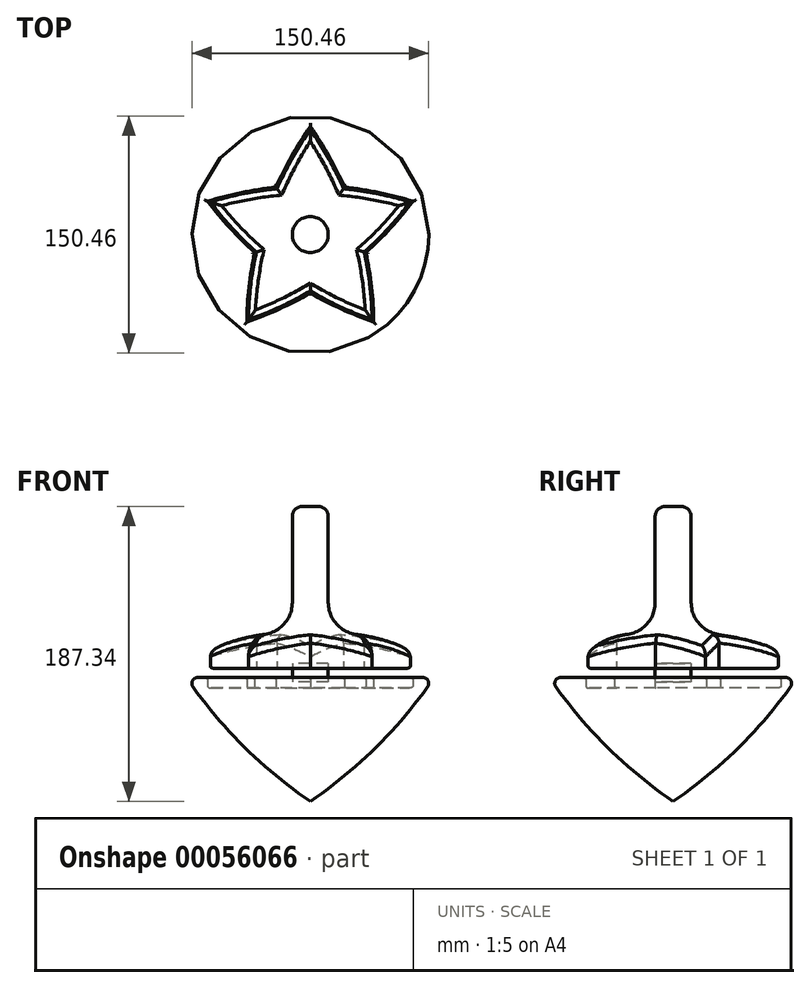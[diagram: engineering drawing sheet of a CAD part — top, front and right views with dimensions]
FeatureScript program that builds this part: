
annotation { "Feature Type Name" : "Feature", "Feature Type Description" : "" }
export const myFeature = defineFeature(function(context is Context, id is Id, definition is map)
    precondition{}
    {
        {
            var Q0;
            Q0=qCreatedBy(makeId("Top.planeOp"),FACE);
            var sketch = newSketch(context, id + "F0", { "sketchPlane" : qUnion([Q0])});
            skArc(sketch, "E0", {"start": v(39.25, -54.02) * mm, "mid": v(28.67, 9.31) * mm, "end": v(0, 66.77) * mm});
            skArc(sketch, "E1", {"start": v(0, 66.77) * mm, "mid": v(-28.67, 9.31) * mm, "end": v(-39.25, -54.02) * mm});
            skArc(sketch, "E2", {"start": v(63.5, 20.63) * mm, "mid": v(0, 30.14) * mm, "end": v(-63.5, 20.63) * mm});
            skArc(sketch, "E3", {"start": v(-63.5, 20.63) * mm, "mid": v(-17.72, -24.39) * mm, "end": v(39.25, -54.02) * mm});
            skArc(sketch, "E4", {"start": v(-39.25, -54.02) * mm, "mid": v(17.72, -24.39) * mm, "end": v(63.5, 20.63) * mm});
            skSolve(sketch);
        }
        {
            var Q0;
            Q0=qSketchRegion(id+"F0",true);
            extrude(context, id + "F1", {"entities" : qUnion([Q0]), "depth" : 67.5 * mm});
        }
        {
            var Q0;
            Q0=qCreatedBy(makeId("Top.planeOp"),FACE);
            var sketch = newSketch(context, id + "F2", { "sketchPlane" : qUnion([Q0])});
            skCircle(sketch, "E5", {"center": v(0, 0) * mm, "radius": 190.5 * mm});
            skLineSegment(sketch, "E6", {"start": v(0, 190.5) * mm, "end": v(0, -190.5) * mm});
            skSolve(sketch);
        }
        {
            var Q0;
            Q0=makeQuery(id+"F1.opExtrude","SWEPT_BODY",BODY,{"disambiguationData":[OSD([sQuery(id+"F0.wireOp",EDGE,"E0"),sQuery(id+"F0.wireOp",EDGE,"E1"),sQuery(id+"F0.wireOp",EDGE,"E2"),sQuery(id+"F0.wireOp",EDGE,"E3"),sQuery(id+"F0.wireOp",EDGE,"E4")])]});
            var Q1;
            Q1=makeQuery(id+"F1.opExtrude","SWEPT_EDGE",EDGE,{"disambiguationData":[OSD([sQuery(id+"F0.wireOp",EDGE,"E2"),sQuery(id+"F0.wireOp",EDGE,"E3")])]});
            var Q2;
            Q2=makeQuery(id+"F1.opExtrude","CAP_FACE",FACE,{"disambiguationData":[OSD([sQuery(id+"F0.wireOp",EDGE,"E0"),sQuery(id+"F0.wireOp",EDGE,"E1"),sQuery(id+"F0.wireOp",EDGE,"E2"),sQuery(id+"F0.wireOp",EDGE,"E3"),sQuery(id+"F0.wireOp",EDGE,"E4")])],"isStart":false});
            transform(context, id + "F3", {"entities" : qUnion([Q0]), "transformType" : TransformType.TRANSLATION_DISTANCE, "transformDirection" : qUnion([Q2]), "distance" : 166.71 * mm, "makeCopy" : false});
        }
        {
            var Q0;
            {var subQ0=sQuery(id+"F2.wireOp",EDGE,"E6");Q0=makeQuery(id+"F2.imprint","IMPRINT",FACE,{"disambiguationData":[TD([[makeQuery(id+"F2.imprint","IMPRINT",EDGE,{"derivedFrom":subQ0}),-1.0]])]});}
            var Q1;
            Q1=sQuery(id+"F2.wireOp",EDGE,"E6");
            revolve(context, id + "F4", {"entities" : qUnion([Q0]), "axis" : qUnion([Q1]), "revolveType" : RevolveType.FULL});
        }
        {
            var Q0;
            Q0=makeQuery(id+"F1.opExtrude","SWEPT_BODY",BODY,{"disambiguationData":[OSD([sQuery(id+"F0.wireOp",EDGE,"E0"),sQuery(id+"F0.wireOp",EDGE,"E1"),sQuery(id+"F0.wireOp",EDGE,"E2"),sQuery(id+"F0.wireOp",EDGE,"E3"),sQuery(id+"F0.wireOp",EDGE,"E4")])]});
            var Q1;
            Q1=makeQuery(id+"F4.opRevolve","SWEPT_BODY",BODY,{"disambiguationData":[OSD([sQuery(id+"F2.wireOp",EDGE,"E5"),sQuery(id+"F2.wireOp",EDGE,"E6")])]});
            booleanBodies(context, id + "F5", {"operationType" : BooleanOperationType.INTERSECTION, "tools" : qUnion([Q0, Q1])});
        }
        {
            var Q0;
            Q0=makeQuery(id+"F5.opBoolean","INTERSECT",BODY,{"derivedFrom":[makeQuery(id+"F1.opExtrude","SWEPT_BODY",BODY,{"disambiguationData":[OSD([sQuery(id+"F0.wireOp",EDGE,"E0"),sQuery(id+"F0.wireOp",EDGE,"E1"),sQuery(id+"F0.wireOp",EDGE,"E2"),sQuery(id+"F0.wireOp",EDGE,"E3"),sQuery(id+"F0.wireOp",EDGE,"E4")])]}),makeQuery(id+"F4.opRevolve","SWEPT_BODY",BODY,{"disambiguationData":[OSD([sQuery(id+"F2.wireOp",EDGE,"E5"),sQuery(id+"F2.wireOp",EDGE,"E6")])]})]});
            var Q1;
            Q1=qCreatedBy(makeId("Top.planeOp"),FACE);
            transform(context, id + "F6", {"entities" : qUnion([Q0]), "transformType" : TransformType.TRANSLATION_DISTANCE, "transformDirection" : qUnion([Q1]), "distance" : 160.87 * mm, "oppositeDirection" : true, "makeCopy" : false});
        }
        {
            var Q0;
            Q0=qCreatedBy(makeId("Top.planeOp"),FACE);
            var sketch = newSketch(context, id + "F7", { "sketchPlane" : qUnion([Q0])});
            skCircle(sketch, "E7", {"center": v(0, 0) * mm, "radius": 19.69 * mm});
            skSolve(sketch);
        }
        {
            var Q0;
            Q0=makeQuery(id+"F7.imprint","IMPRINT",FACE,{"disambiguationData":[TD([[makeQuery(id+"F7.imprint","IMPRINT",EDGE,{"derivedFrom":sQuery(id+"F7.wireOp",EDGE,"E7")}),1.0]])]});
            var Q1;
            Q1=sQuery(id+"F7.wireOp",EDGE,"E7");
            extrude(context, id + "F8", {"entities" : qUnion([Q0]), "surfaceEntities" : qUnion([Q1]), "depth" : 6.35 * mm});
        }
        {
            var Q0;
            Q0=makeQuery(id+"F8.opExtrude","SWEPT_BODY",BODY,{"disambiguationData":[OSD([sQuery(id+"F7.wireOp",EDGE,"E7")])]});
            var Q1;
            Q1=makeQuery(id+"F1.opExtrude","CAP_FACE",FACE,{"disambiguationData":[OSD([sQuery(id+"F0.wireOp",EDGE,"E0"),sQuery(id+"F0.wireOp",EDGE,"E1"),sQuery(id+"F0.wireOp",EDGE,"E2"),sQuery(id+"F0.wireOp",EDGE,"E3"),sQuery(id+"F0.wireOp",EDGE,"E4")])],"isStart":true});
            transform(context, id + "F9", {"entities" : qUnion([Q0]), "transformType" : TransformType.TRANSLATION_DISTANCE, "transformDirection" : qUnion([Q1]), "distance" : 52.24 * mm, "makeCopy" : false});
        }
        {
            var Q0;
            Q0=makeQuery(id+"F8.opExtrude","SWEPT_BODY",BODY,{"disambiguationData":[OSD([sQuery(id+"F7.wireOp",EDGE,"E7")])]});
            var Q1;
            Q1=makeQuery(id+"F5.opBoolean","INTERSECT",BODY,{"derivedFrom":[makeQuery(id+"F1.opExtrude","SWEPT_BODY",BODY,{"disambiguationData":[OSD([sQuery(id+"F0.wireOp",EDGE,"E0"),sQuery(id+"F0.wireOp",EDGE,"E1"),sQuery(id+"F0.wireOp",EDGE,"E2"),sQuery(id+"F0.wireOp",EDGE,"E3"),sQuery(id+"F0.wireOp",EDGE,"E4")])]}),makeQuery(id+"F4.opRevolve","SWEPT_BODY",BODY,{"disambiguationData":[OSD([sQuery(id+"F2.wireOp",EDGE,"E5"),sQuery(id+"F2.wireOp",EDGE,"E6")])]})]});
            booleanBodies(context, id + "F10", {"operationType" : BooleanOperationType.SUBTRACTION, "tools" : qUnion([Q0]), "targets" : qUnion([Q1])});
        }
        {
            var Q0;
            Q0=qCreatedBy(makeId("Front.planeOp"),FACE);
            var sketch = newSketch(context, id + "F11", { "sketchPlane" : qUnion([Q0])});
            skLineSegment(sketch, "E8", {"start": v(-78.74, 0) * mm, "end": v(78.74, 0) * mm});
            skArc(sketch, "E9", {"start": v(-78.74, 0) * mm, "mid": v(-43.07, -43.07) * mm, "end": v(0, -78.74) * mm});
            skLineSegment(sketch, "E10", {"start": v(0, -78.74) * mm, "end": v(0, 0) * mm});
            skSolve(sketch);
        }
        {
            var Q0;
            {var subQ0=sQuery(id+"F11.wireOp",EDGE,"E9");Q0=makeQuery(id+"F11.imprint","IMPRINT",FACE,{"disambiguationData":[TD([[makeQuery(id+"F11.imprint","IMPRINT",EDGE,{"derivedFrom":subQ0}),1.0]])]});}
            var Q1;
            Q1=sQuery(id+"F11.wireOp",EDGE,"E10");
            revolve(context, id + "F12", {"operationType" : NewBodyOperationType.ADD, "entities" : qUnion([Q0]), "axis" : qUnion([Q1]), "revolveType" : RevolveType.FULL});
        }
        {
            var Q0;
            Q0=qCreatedBy(makeId("Top.planeOp"),FACE);
            var sketch = newSketch(context, id + "F13", { "sketchPlane" : qUnion([Q0])});
            skCircle(sketch, "E11", {"center": v(0, 0) * mm, "radius": 11.43 * mm});
            skSolve(sketch);
        }
        {
            var Q0;
            Q0=makeQuery(id+"F13.imprint","IMPRINT",FACE,{"disambiguationData":[TD([[makeQuery(id+"F13.imprint","IMPRINT",EDGE,{"derivedFrom":sQuery(id+"F13.wireOp",EDGE,"E11")}),1.0]])]});
            extrude(context, id + "F14", {"entities" : qUnion([Q0]), "operationType" : NewBodyOperationType.ADD, "depth" : 108.6 * mm, "hasSecondDirection" : true, "secondDirectionOppositeDirection" : false, "secondDirectionDepth" : 8.63 * mm});
        }
        {
            var Q0;
            Q0=makeQuery(id+"F14.opExtrude","CAP_EDGE",EDGE,{"disambiguationData":[OSD([sQuery(id+"F13.wireOp",EDGE,"E11")])],"isStart":false});
            fillet(context, id + "F15", {"entities" : qUnion([Q0]), "radius" : 6.35 * mm, "tangentPropagation" : true, "allowEdgeOverflow" : false});
        }
        {
            var Q0;
            Q0=makeQuery(id+"F13.imprint","IMPRINT",FACE,{"disambiguationData":[TD([[makeQuery(id+"F13.imprint","IMPRINT",EDGE,{"derivedFrom":sQuery(id+"F13.wireOp",EDGE,"E11")}),1.0]])]});
            extrude(context, id + "F16", {"entities" : qUnion([Q0]), "depth" : 11.77 * mm});
        }
        {
            var Q0;
            Q0=makeQuery(id+"F16.opExtrude","SWEPT_BODY",BODY,{"disambiguationData":[OSD([sQuery(id+"F13.wireOp",EDGE,"E11")])]});
            transform(context, id + "F17", {"entities" : qUnion([Q0]), "transformType" : TransformType.TRANSLATION_3D, "dx" : 0 * mm, "dy" : 0 * mm, "dz" : -2.9 * mm, "makeCopy" : false});
        }
        {
            var Q0;
            Q0=makeQuery(id+"F16.opExtrude","SWEPT_BODY",BODY,{"disambiguationData":[OSD([sQuery(id+"F13.wireOp",EDGE,"E11")])]});
            transform(context, id + "F18", {"entities" : qUnion([Q0]), "transformType" : TransformType.TRANSLATION_3D, "dx" : 0 * mm, "dy" : 0 * mm, "dz" : 0 * mm, "makeCopy" : true});
        }
        {
            var Q0;
            Q0=makeQuery(id+"F5.opBoolean","INTERSECT",BODY,{"derivedFrom":[makeQuery(id+"F1.opExtrude","SWEPT_BODY",BODY,{"disambiguationData":[OSD([sQuery(id+"F0.wireOp",EDGE,"E0"),sQuery(id+"F0.wireOp",EDGE,"E1"),sQuery(id+"F0.wireOp",EDGE,"E2"),sQuery(id+"F0.wireOp",EDGE,"E3"),sQuery(id+"F0.wireOp",EDGE,"E4")])]}),makeQuery(id+"F4.opRevolve","SWEPT_BODY",BODY,{"disambiguationData":[OSD([sQuery(id+"F2.wireOp",EDGE,"E5"),sQuery(id+"F2.wireOp",EDGE,"E6")])]})]});
            transform(context, id + "F19", {"entities" : qUnion([Q0]), "transformType" : TransformType.TRANSLATION_3D, "dx" : 0 * mm, "dy" : 0 * mm, "dz" : -11.54 * mm, "makeCopy" : true});
        }
        {
            var Q0;
            Q0=makeQuery(id+"F19.opPattern","COPY",BODY,{"derivedFrom":makeQuery(id+"F5.opBoolean","INTERSECT",BODY,{"derivedFrom":[makeQuery(id+"F1.opExtrude","SWEPT_BODY",BODY,{"disambiguationData":[OSD([sQuery(id+"F0.wireOp",EDGE,"E0"),sQuery(id+"F0.wireOp",EDGE,"E1"),sQuery(id+"F0.wireOp",EDGE,"E2"),sQuery(id+"F0.wireOp",EDGE,"E3"),sQuery(id+"F0.wireOp",EDGE,"E4")])]}),makeQuery(id+"F4.opRevolve","SWEPT_BODY",BODY,{"disambiguationData":[OSD([sQuery(id+"F2.wireOp",EDGE,"E5"),sQuery(id+"F2.wireOp",EDGE,"E6")])]})]}),"instanceName":"1"});
            var Q1;
            Q1=makeQuery(id+"F12.opRevolve","SWEPT_BODY",BODY,{"disambiguationData":[OSD([sQuery(id+"F11.wireOp",EDGE,"E8"),sQuery(id+"F11.wireOp",EDGE,"E9"),sQuery(id+"F11.wireOp",EDGE,"E10")])]});
            var Q2;
            Q2=makeQuery(id+"F19.opPattern","COPY",FACE,{"derivedFrom":makeQuery(id+"F1.opExtrude","CAP_FACE",FACE,{"disambiguationData":[OSD([sQuery(id+"F0.wireOp",EDGE,"E0"),sQuery(id+"F0.wireOp",EDGE,"E1"),sQuery(id+"F0.wireOp",EDGE,"E2"),sQuery(id+"F0.wireOp",EDGE,"E3"),sQuery(id+"F0.wireOp",EDGE,"E4")])],"isStart":true}),"instanceName":"1"});
            booleanBodies(context, id + "F20", {"operationType" : BooleanOperationType.SUBTRACTION, "tools" : qUnion([Q0]), "targets" : qUnion([Q1]), "offset" : true, "offsetAll" : true, "entitiesToOffset" : qUnion([Q2]), "offsetDistance" : 1.02 * mm});
        }
        {
            var Q0;
            Q0=makeQuery(id+"F12.opRevolve","SWEPT_EDGE",EDGE,{"disambiguationData":[OSD([sQuery(id+"F11.wireOp",EDGE,"E8"),sQuery(id+"F11.wireOp",EDGE,"E9")])]});
            fillet(context, id + "F21", {"entities" : qUnion([Q0]), "radius" : 3.8 * mm, "tangentPropagation" : true, "allowEdgeOverflow" : false});
        }
        {
            var Q0;
            {var subQ0=sQuery(id+"F0.wireOp",EDGE,"E3");Q0=makeQuery(id+"F5.opBoolean","INTERSECT",EDGE,{"derivedFrom":[makeQuery(id+"F1.opExtrude","SWEPT_FACE",FACE,{"disambiguationData":[OSD([subQ0]),TDD([makeQuery(id+"F0.imprint","IMPRINT",EDGE,{"disambiguationData":[TD([[makeQuery(id+"F0.imprint","INTERSECT",VERTEX,{"derivedFrom":[sQuery(id+"F0.wireOp",EDGE,"E2"),subQ0]}),-1.0]])],"derivedFrom":subQ0})])]}),makeQuery(id+"F4.opRevolve","SWEPT_FACE",FACE,{"disambiguationData":[OSD([sQuery(id+"F2.wireOp",EDGE,"E5")])]})]});}
            var Q1;
            {var subQ0=sQuery(id+"F0.wireOp",EDGE,"E2");Q1=makeQuery(id+"F5.opBoolean","INTERSECT",EDGE,{"derivedFrom":[makeQuery(id+"F1.opExtrude","SWEPT_FACE",FACE,{"disambiguationData":[OSD([subQ0]),TDD([makeQuery(id+"F0.imprint","IMPRINT",EDGE,{"disambiguationData":[TD([[makeQuery(id+"F0.imprint","INTERSECT",VERTEX,{"derivedFrom":[subQ0,sQuery(id+"F0.wireOp",EDGE,"E3")]}),1.0]])],"derivedFrom":subQ0})])]}),makeQuery(id+"F4.opRevolve","SWEPT_FACE",FACE,{"disambiguationData":[OSD([sQuery(id+"F2.wireOp",EDGE,"E5")])]})]});}
            var Q2;
            {var subQ0=sQuery(id+"F0.wireOp",EDGE,"E1");Q2=makeQuery(id+"F5.opBoolean","INTERSECT",EDGE,{"derivedFrom":[makeQuery(id+"F1.opExtrude","SWEPT_FACE",FACE,{"disambiguationData":[OSD([subQ0]),TDD([makeQuery(id+"F0.imprint","IMPRINT",EDGE,{"disambiguationData":[TD([[makeQuery(id+"F0.imprint","INTERSECT",VERTEX,{"derivedFrom":[subQ0,sQuery(id+"F0.wireOp",EDGE,"E4")]}),1.0]])],"derivedFrom":subQ0})])]}),makeQuery(id+"F4.opRevolve","SWEPT_FACE",FACE,{"disambiguationData":[OSD([sQuery(id+"F2.wireOp",EDGE,"E5")])]})]});}
            var Q3;
            {var subQ0=sQuery(id+"F0.wireOp",EDGE,"E4");Q3=makeQuery(id+"F5.opBoolean","INTERSECT",EDGE,{"derivedFrom":[makeQuery(id+"F1.opExtrude","SWEPT_FACE",FACE,{"disambiguationData":[OSD([subQ0]),TDD([makeQuery(id+"F0.imprint","IMPRINT",EDGE,{"disambiguationData":[TD([[makeQuery(id+"F0.imprint","INTERSECT",VERTEX,{"derivedFrom":[sQuery(id+"F0.wireOp",EDGE,"E1"),subQ0]}),-1.0]])],"derivedFrom":subQ0})])]}),makeQuery(id+"F4.opRevolve","SWEPT_FACE",FACE,{"disambiguationData":[OSD([sQuery(id+"F2.wireOp",EDGE,"E5")])]})]});}
            var Q4;
            {var subQ0=sQuery(id+"F0.wireOp",EDGE,"E3");Q4=makeQuery(id+"F5.opBoolean","INTERSECT",EDGE,{"derivedFrom":[makeQuery(id+"F1.opExtrude","SWEPT_FACE",FACE,{"disambiguationData":[OSD([subQ0]),TDD([makeQuery(id+"F0.imprint","IMPRINT",EDGE,{"disambiguationData":[TD([[makeQuery(id+"F0.imprint","INTERSECT",VERTEX,{"derivedFrom":[sQuery(id+"F0.wireOp",EDGE,"E0"),subQ0]}),1.0]])],"derivedFrom":subQ0})])]}),makeQuery(id+"F4.opRevolve","SWEPT_FACE",FACE,{"disambiguationData":[OSD([sQuery(id+"F2.wireOp",EDGE,"E5")])]})]});}
            var Q5;
            {var subQ0=sQuery(id+"F0.wireOp",EDGE,"E0");Q5=makeQuery(id+"F5.opBoolean","INTERSECT",EDGE,{"derivedFrom":[makeQuery(id+"F1.opExtrude","SWEPT_FACE",FACE,{"disambiguationData":[OSD([subQ0]),TDD([makeQuery(id+"F0.imprint","IMPRINT",EDGE,{"disambiguationData":[TD([[makeQuery(id+"F0.imprint","INTERSECT",VERTEX,{"derivedFrom":[subQ0,sQuery(id+"F0.wireOp",EDGE,"E3")]}),-1.0]])],"derivedFrom":subQ0})])]}),makeQuery(id+"F4.opRevolve","SWEPT_FACE",FACE,{"disambiguationData":[OSD([sQuery(id+"F2.wireOp",EDGE,"E5")])]})]});}
            var Q6;
            {var subQ0=sQuery(id+"F0.wireOp",EDGE,"E4");Q6=makeQuery(id+"F5.opBoolean","INTERSECT",EDGE,{"derivedFrom":[makeQuery(id+"F1.opExtrude","SWEPT_FACE",FACE,{"disambiguationData":[OSD([subQ0]),TDD([makeQuery(id+"F0.imprint","IMPRINT",EDGE,{"disambiguationData":[TD([[makeQuery(id+"F0.imprint","INTERSECT",VERTEX,{"derivedFrom":[sQuery(id+"F0.wireOp",EDGE,"E2"),subQ0]}),1.0]])],"derivedFrom":subQ0})])]}),makeQuery(id+"F4.opRevolve","SWEPT_FACE",FACE,{"disambiguationData":[OSD([sQuery(id+"F2.wireOp",EDGE,"E5")])]})]});}
            var Q7;
            {var subQ0=sQuery(id+"F0.wireOp",EDGE,"E2");Q7=makeQuery(id+"F5.opBoolean","INTERSECT",EDGE,{"derivedFrom":[makeQuery(id+"F1.opExtrude","SWEPT_FACE",FACE,{"disambiguationData":[OSD([subQ0]),TDD([makeQuery(id+"F0.imprint","IMPRINT",EDGE,{"disambiguationData":[TD([[makeQuery(id+"F0.imprint","INTERSECT",VERTEX,{"derivedFrom":[subQ0,sQuery(id+"F0.wireOp",EDGE,"E4")]}),-1.0]])],"derivedFrom":subQ0})])]}),makeQuery(id+"F4.opRevolve","SWEPT_FACE",FACE,{"disambiguationData":[OSD([sQuery(id+"F2.wireOp",EDGE,"E5")])]})]});}
            var Q8;
            {var subQ0=sQuery(id+"F0.wireOp",EDGE,"E0");Q8=makeQuery(id+"F5.opBoolean","INTERSECT",EDGE,{"derivedFrom":[makeQuery(id+"F1.opExtrude","SWEPT_FACE",FACE,{"disambiguationData":[OSD([subQ0]),TDD([makeQuery(id+"F0.imprint","IMPRINT",EDGE,{"disambiguationData":[TD([[makeQuery(id+"F0.imprint","INTERSECT",VERTEX,{"derivedFrom":[subQ0,sQuery(id+"F0.wireOp",EDGE,"E1")]}),1.0]])],"derivedFrom":subQ0})])]}),makeQuery(id+"F4.opRevolve","SWEPT_FACE",FACE,{"disambiguationData":[OSD([sQuery(id+"F2.wireOp",EDGE,"E5")])]})]});}
            var Q9;
            {var subQ0=sQuery(id+"F0.wireOp",EDGE,"E1");Q9=makeQuery(id+"F5.opBoolean","INTERSECT",EDGE,{"derivedFrom":[makeQuery(id+"F1.opExtrude","SWEPT_FACE",FACE,{"disambiguationData":[OSD([subQ0]),TDD([makeQuery(id+"F0.imprint","IMPRINT",EDGE,{"disambiguationData":[TD([[makeQuery(id+"F0.imprint","INTERSECT",VERTEX,{"derivedFrom":[sQuery(id+"F0.wireOp",EDGE,"E0"),subQ0]}),-1.0]])],"derivedFrom":subQ0})])]}),makeQuery(id+"F4.opRevolve","SWEPT_FACE",FACE,{"disambiguationData":[OSD([sQuery(id+"F2.wireOp",EDGE,"E5")])]})]});}
            fillet(context, id + "F22", {"entities" : qUnion([Q0, Q1, Q2, Q3, Q4, Q5, Q6, Q7, Q8, Q9]), "radius" : 5.08 * mm, "tangentPropagation" : true, "allowEdgeOverflow" : false});
        }
        {
            var Q0;
            Q0=makeQuery(id+"F1.opExtrude","CAP_FACE",FACE,{"disambiguationData":[OSD([sQuery(id+"F0.wireOp",EDGE,"E0"),sQuery(id+"F0.wireOp",EDGE,"E1"),sQuery(id+"F0.wireOp",EDGE,"E2"),sQuery(id+"F0.wireOp",EDGE,"E3"),sQuery(id+"F0.wireOp",EDGE,"E4")])],"isStart":true});
            fillet(context, id + "F23", {"entities" : qUnion([Q0]), "radius" : 1.27 * mm, "tangentPropagation" : true, "allowEdgeOverflow" : false});
        }
        {
            var Q0;
            Q0=makeQuery(id+"F20.tempBoolean.opBoolean","COPY",FACE,{"derivedFrom":makeQuery(id+"F20.offsetTempBody.opPattern","COPY",FACE,{"derivedFrom":makeQuery(id+"F19.opPattern","COPY",FACE,{"derivedFrom":makeQuery(id+"F1.opExtrude","CAP_FACE",FACE,{"disambiguationData":[OSD([sQuery(id+"F0.wireOp",EDGE,"E0"),sQuery(id+"F0.wireOp",EDGE,"E1"),sQuery(id+"F0.wireOp",EDGE,"E2"),sQuery(id+"F0.wireOp",EDGE,"E3"),sQuery(id+"F0.wireOp",EDGE,"E4")])],"isStart":true}),"instanceName":"1"}),"instanceName":"1"})});
            var Q1;
            Q1=makeQuery(id+"F12.opRevolve","SWEPT_FACE",FACE,{"disambiguationData":[OSD([sQuery(id+"F11.wireOp",EDGE,"E8")])]});
            fillet(context, id + "F24", {"entities" : qUnion([Q0, Q1]), "radius" : 1.27 * mm, "tangentPropagation" : true, "allowEdgeOverflow" : false});
        }
        {
            var Q0;
            Q0=makeQuery(id+"F14.boolean.opBoolean","INTERSECT",EDGE,{"derivedFrom":[makeQuery(id+"F4.opRevolve","SWEPT_FACE",FACE,{"disambiguationData":[OSD([sQuery(id+"F2.wireOp",EDGE,"E5")])]}),makeQuery(id+"F14.opExtrude","SWEPT_FACE",FACE,{"disambiguationData":[OSD([sQuery(id+"F13.wireOp",EDGE,"E11")])]})]});
            fillet(context, id + "F25", {"entities" : qUnion([Q0]), "radius" : 20.32 * mm, "tangentPropagation" : true, "allowEdgeOverflow" : false});
        }
    });
